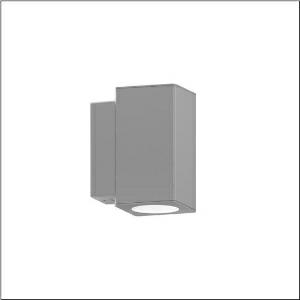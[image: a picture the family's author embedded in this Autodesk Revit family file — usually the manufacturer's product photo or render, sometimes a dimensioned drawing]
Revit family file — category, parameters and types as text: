
# Revit family: cl_31_wand_5cl563623
name_source: partatom
category: Lighting Fixtures
units: mm (PartAtom-declared; Revit-internal decimal feet)

## family parameters
Cut with Voids When Loaded = No
Host = Face
Light Source = No
Part Type = Normal
Room Calculation Point = No
Round Connector Dimension = Use Diameter
Shared = No

## types (1)
- --- (1 x LED, 600 lm, 5.4 W, 3000K)
    Apparent Load = 5 VA
    CIE Flux Codes = 98 100 100 50 100
    Color Rendering = 80
    Color Temperature = 3000K
    Default Elevation = 1800 mm
    Description = CL 31 Wall, wall luminaire, primary light control with reflector, of aluminium, primary optical cover: cover panel, of glass, transparent, light emission: up/down distribution, primary light characteristic: symmetric, installation type: surface-mounted, for 2x LED, rated luminous flux: 300lm, luminous efficacy: 110lm/W, light colour: 830, colour temperature: 3000K, control gear: ECG DALI, with terminal, 5-pole, max. 2.5mm², mains connection: 220..240V, AC, 50/60Hz, rated input power: 5.5W, luminaire housing, square, of aluminium, powder-coated, Siteco® metallic grey, length: 143mm, width: 100mm, height: 186mm, protection rating (complete): IP65, insulation class (complete): insulation class I (protective earthing), certification: CE, ENEC, impact resistance: IK08, permissible operating ambient temperature for outdoor applications: -20..+50°C, packaging unit: 1 piece
    Height = 186 mm
    Lamp = 1 x LED
    Lamp Light Flux = 600 lm
    Lamp Power = 5.4 W
    Lamp count = 1
    Length = 100 mm  [stored 0.328084 ft]
    Luminous efficacy = 111 lm/W
    Manufacturer = Siteco
    ModVariant = No
    Model = 5CL563623
    Mounting Place = Wall
    Mounting Type = Surface mounted
    Number of Poles = 1
    OnlyDefault = Yes
    Power Factor = 1
    Product Name = CL 31 Wand
    Product group = wall luminaire
    ProductGroupID = 2001
    Protection Class = Protection class I
    Protection Degree = IP 65
    RLX_Detail_Level = 1
    RlxData = <blob elided: 40405 chars, md5=10fd8257>
    Socket = socket
    Standby Power = 0 W
    System Light Flux = 600 lm
    System Power = 5 W
    Type Comments = factory setting: luminous flux: 100 % | dim-lin: 254 | 135 mA
    Type Image = l_1006895.jpg
    URL = http://relux.com
    VarID = @adj_117155
    Voltage = 0 V
    Weight = 0.00 kg
    Width = 143 mm

note: [stored X ft] marks values corroborated as IEEE doubles in the binary element streams (Revit-internal decimal feet)

## geometry (parser evidence)
native form markers: Blend x4, Sweep x13
no freeform markers — native parametric forms only
